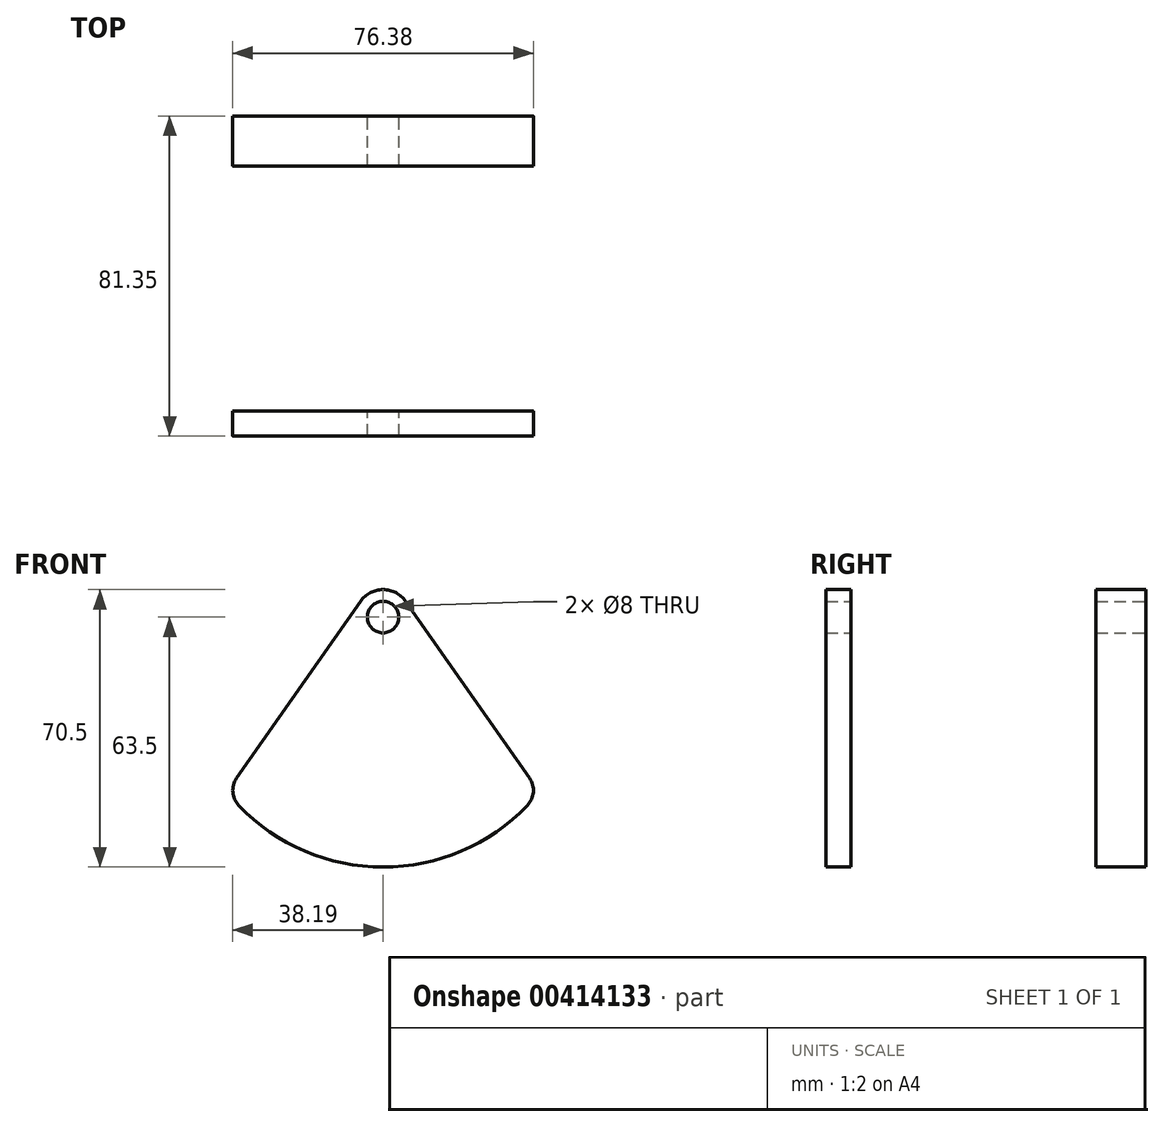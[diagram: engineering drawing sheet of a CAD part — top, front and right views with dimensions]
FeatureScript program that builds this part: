
annotation { "Feature Type Name" : "Feature", "Feature Type Description" : "" }
export const myFeature = defineFeature(function(context is Context, id is Id, definition is map)
    precondition{}
    {
        {
            var Q0;
            Q0=qCreatedBy(makeId("Front.planeOp"),FACE);
            var sketch = newSketch(context, id + "F0", { "sketchPlane" : qUnion([Q0])});
            skCircle(sketch, "E0", {"center": v(0, 0) * mm, "radius": 4 * mm});
            skArc(sketch, "E1", {"start": v(-5.73, 4.02) * mm, "mid": v(-3.23, 6.2) * mm, "end": v(0, 7) * mm});
            skLineSegment(sketch, "E2", {"start": v(-20.9, 7) * mm, "end": v(41.08, 7) * mm, "construction": true});
            skLineSegment(sketch, "E3", {"start": v(-53.33, -63.5) * mm, "end": v(53.33, -63.5) * mm, "construction": true});
            skArc(sketch, "E4.MirrorCS", {"start": v(5.73, 4.02) * mm, "mid": v(3.23, 6.2) * mm, "end": v(0, 7) * mm});
            skLineSegment(sketch, "E5", {"start": v(-5.73, 4.02) * mm, "end": v(-37.2, -40.91) * mm});
            skArc(sketch, "E6", {"start": v(-37.2, -40.91) * mm, "mid": v(-38.17, -44.49) * mm, "end": v(-36.65, -47.87) * mm});
            skArc(sketch, "E7", {"start": v(-36.65, -47.87) * mm, "mid": v(-19.92, -59.43) * mm, "end": v(0, -63.5) * mm});
            skPoint(sketch, "E7.endSnap0", {"position": v(0, -63.5) * mm});
            skArc(sketch, "E8.MirrorCS", {"start": v(36.65, -47.87) * mm, "mid": v(19.92, -59.43) * mm, "end": v(0, -63.5) * mm});
            skArc(sketch, "E9.MirrorCS", {"start": v(37.2, -40.91) * mm, "mid": v(38.17, -44.49) * mm, "end": v(36.65, -47.87) * mm});
            skLineSegment(sketch, "E10.MirrorCS", {"start": v(5.73, 4.02) * mm, "end": v(37.2, -40.91) * mm});
            skSolve(sketch);
        }
        {
            var Q0;
            Q0 = qSketchRegion(id + "F0", true);
            extrude(context, id + "F1", {"entities" : qUnion([Q0]), "depth" : 12.7 * mm});
        }
        {
            var Q0;
            Q0=qCreatedBy(makeId("Front.planeOp"),FACE);
            cPlane(context, id + "F2", {"entities" : qUnion([Q0]), "cplaneType" : CPlaneType.OFFSET, "offset" : 75 * mm, "width" : 150 * mm, "height" : 150 * mm});
        }
        {
            var Q0;
            Q0=qCreatedBy(id+"F2.planeOp",FACE);
            var sketch = newSketch(context, id + "F3", { "sketchPlane" : qUnion([Q0])});
            skLineSegment(sketch, "E11.0.0", {"start": v(37.2, -40.91) * mm, "end": v(5.73, 4.02) * mm});
            skArc(sketch, "E11.0.1", {"start": v(5.73, 4.02) * mm, "mid": v(0, 7) * mm, "end": v(-5.73, 4.02) * mm});
            skLineSegment(sketch, "E11.0.2", {"start": v(-5.73, 4.02) * mm, "end": v(-37.2, -40.91) * mm});
            skArc(sketch, "E11.0.3", {"start": v(-37.2, -40.91) * mm, "mid": v(-38.17, -44.49) * mm, "end": v(-36.65, -47.87) * mm});
            skArc(sketch, "E11.0.4", {"start": v(-36.65, -47.87) * mm, "mid": v(0, -63.5) * mm, "end": v(36.65, -47.87) * mm});
            skArc(sketch, "E11.0.5", {"start": v(36.65, -47.87) * mm, "mid": v(38.17, -44.49) * mm, "end": v(37.2, -40.91) * mm});
            skCircle(sketch, "E12.0", {"center": v(0, 0) * mm, "radius": 4 * mm});
            skSolve(sketch);
        }
        {
            var Q0;
            Q0 = qSketchRegion(id + "F3", true);
            extrude(context, id + "F4", {"entities" : qUnion([Q0]), "depth" : 6.35 * mm});
        }
    });
